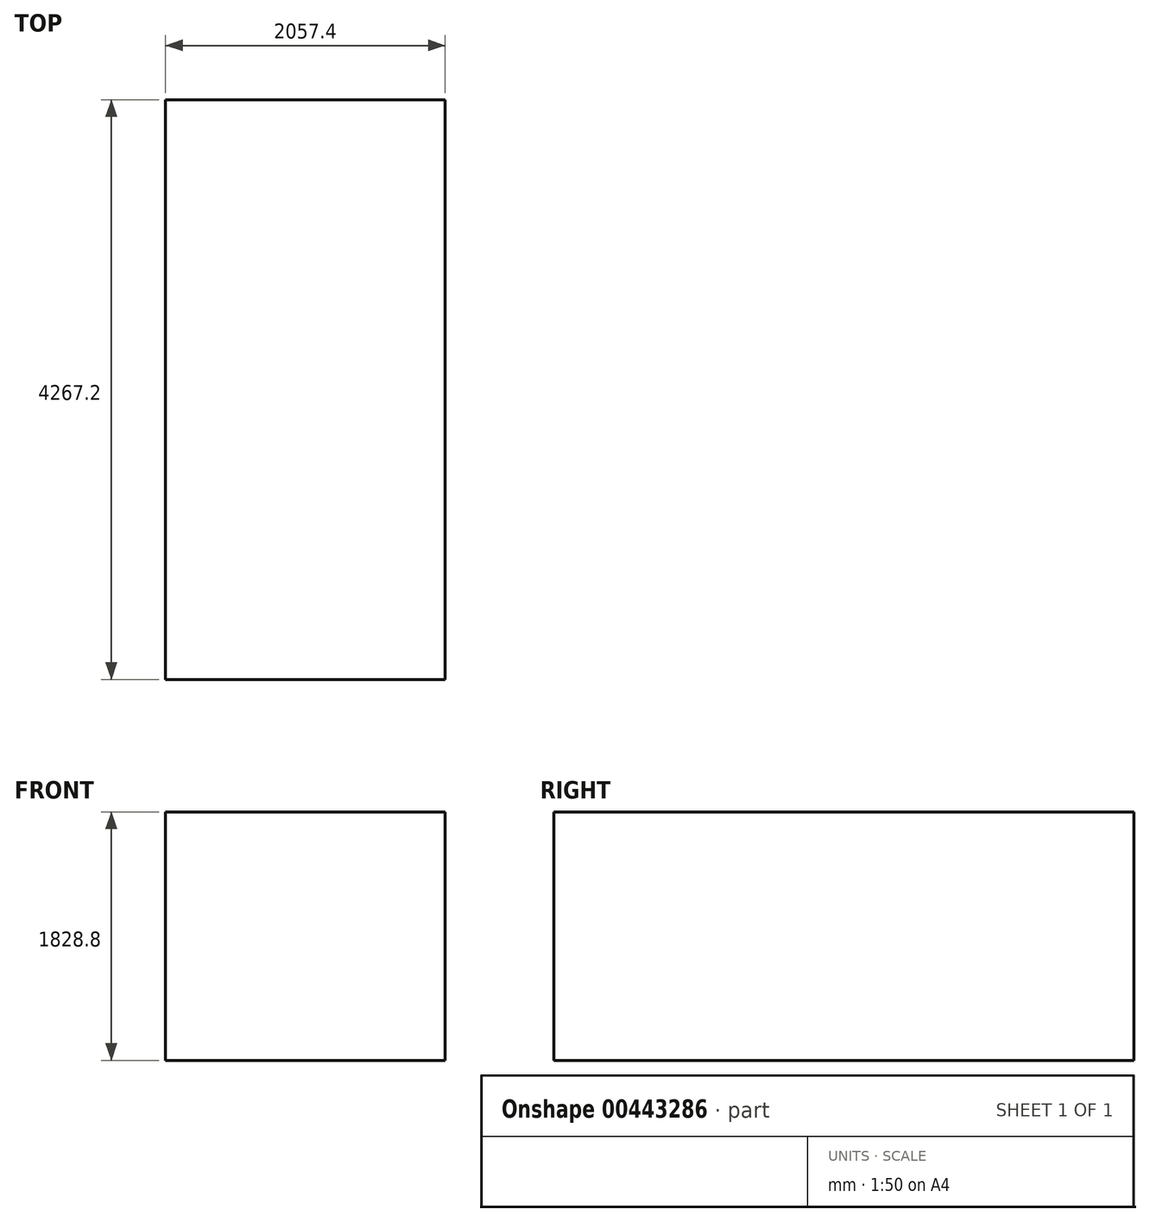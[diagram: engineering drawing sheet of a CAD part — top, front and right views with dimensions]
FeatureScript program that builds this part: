
annotation { "Feature Type Name" : "Feature", "Feature Type Description" : "" }
export const myFeature = defineFeature(function(context is Context, id is Id, definition is map)
    precondition{}
    {
        {
            var Q0;
            Q0=qCreatedBy(makeId("Top.planeOp"),FACE);
            var sketch = newSketch(context, id + "F0", { "sketchPlane" : qUnion([Q0])});
            skLineSegment(sketch, "E0.bottom", {"start": v(1028.7, 2133.6) * mm, "end": v(-1028.7, 2133.6) * mm});
            skLineSegment(sketch, "E0.top", {"start": v(1028.7, -2133.6) * mm, "end": v(-1028.7, -2133.6) * mm});
            skLineSegment(sketch, "E0.left", {"start": v(1028.7, 2133.6) * mm, "end": v(1028.7, -2133.6) * mm});
            skLineSegment(sketch, "E0.right", {"start": v(-1028.7, 2133.6) * mm, "end": v(-1028.7, -2133.6) * mm});
            skPoint(sketch, "E0.middle", {"position": v(0, 0) * mm});
            skSolve(sketch);
        }
        {
            var Q0;
            Q0 = qSketchRegion(id + "F0", true);
            extrude(context, id + "F1", {"entities" : qUnion([Q0]), "depth" : 1828.8 * mm});
        }
    });
